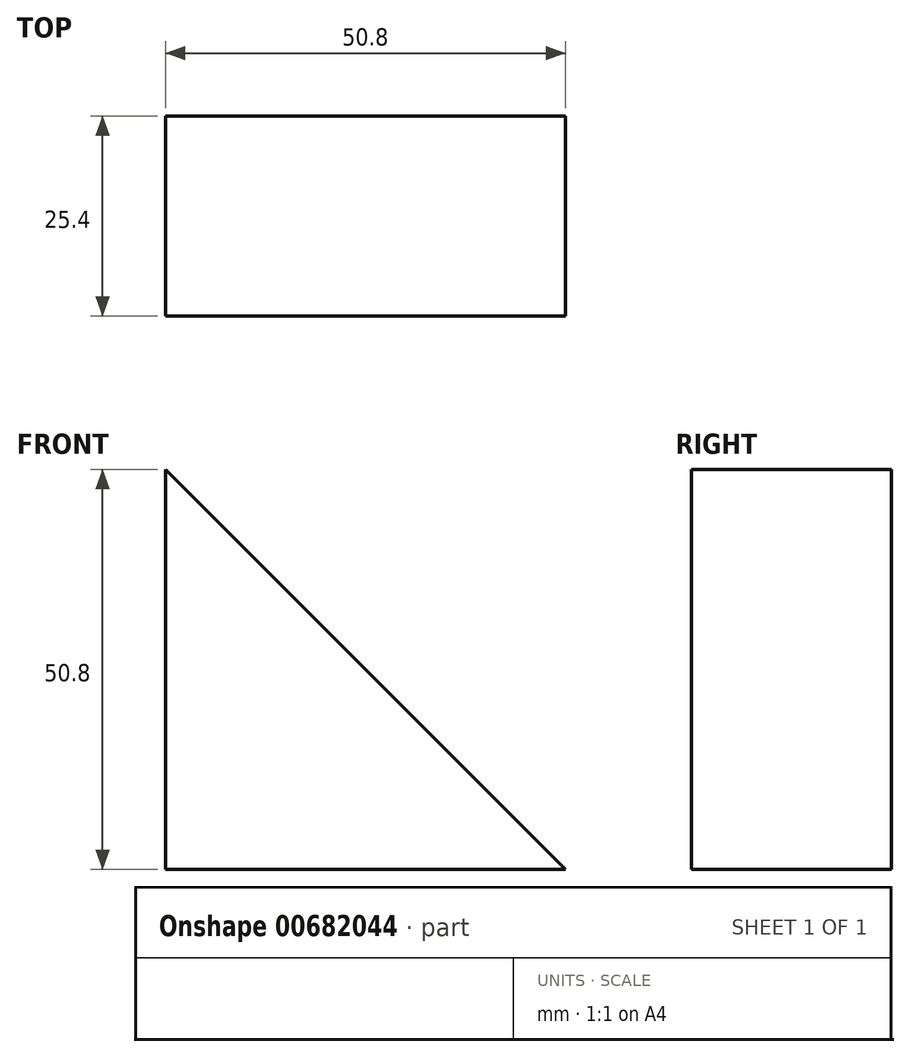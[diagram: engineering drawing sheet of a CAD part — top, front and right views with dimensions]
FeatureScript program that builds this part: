
annotation { "Feature Type Name" : "Feature", "Feature Type Description" : "" }
export const myFeature = defineFeature(function(context is Context, id is Id, definition is map)
    precondition{}
    {
        {
            var Q0;
            Q0=qCreatedBy(makeId("Front.planeOp"),FACE);
            var sketch = newSketch(context, id + "F0", { "sketchPlane" : qUnion([Q0])});
            skLineSegment(sketch, "E0", {"start": v(0, 0) * mm, "end": v(-50.8, 0) * mm});
            skLineSegment(sketch, "E1", {"start": v(-50.8, 0) * mm, "end": v(-50.8, 50.8) * mm});
            skLineSegment(sketch, "E2", {"start": v(-50.8, 50.8) * mm, "end": v(0, 0) * mm});
            skSolve(sketch);
        }
        {
            var Q0;
            Q0 = qSketchRegion(id + "F0", true);
            extrude(context, id + "F1", {"entities" : qUnion([Q0]), "depth" : 25.4 * mm, "offsetDistance" : 25.4 * mm});
        }
    });
